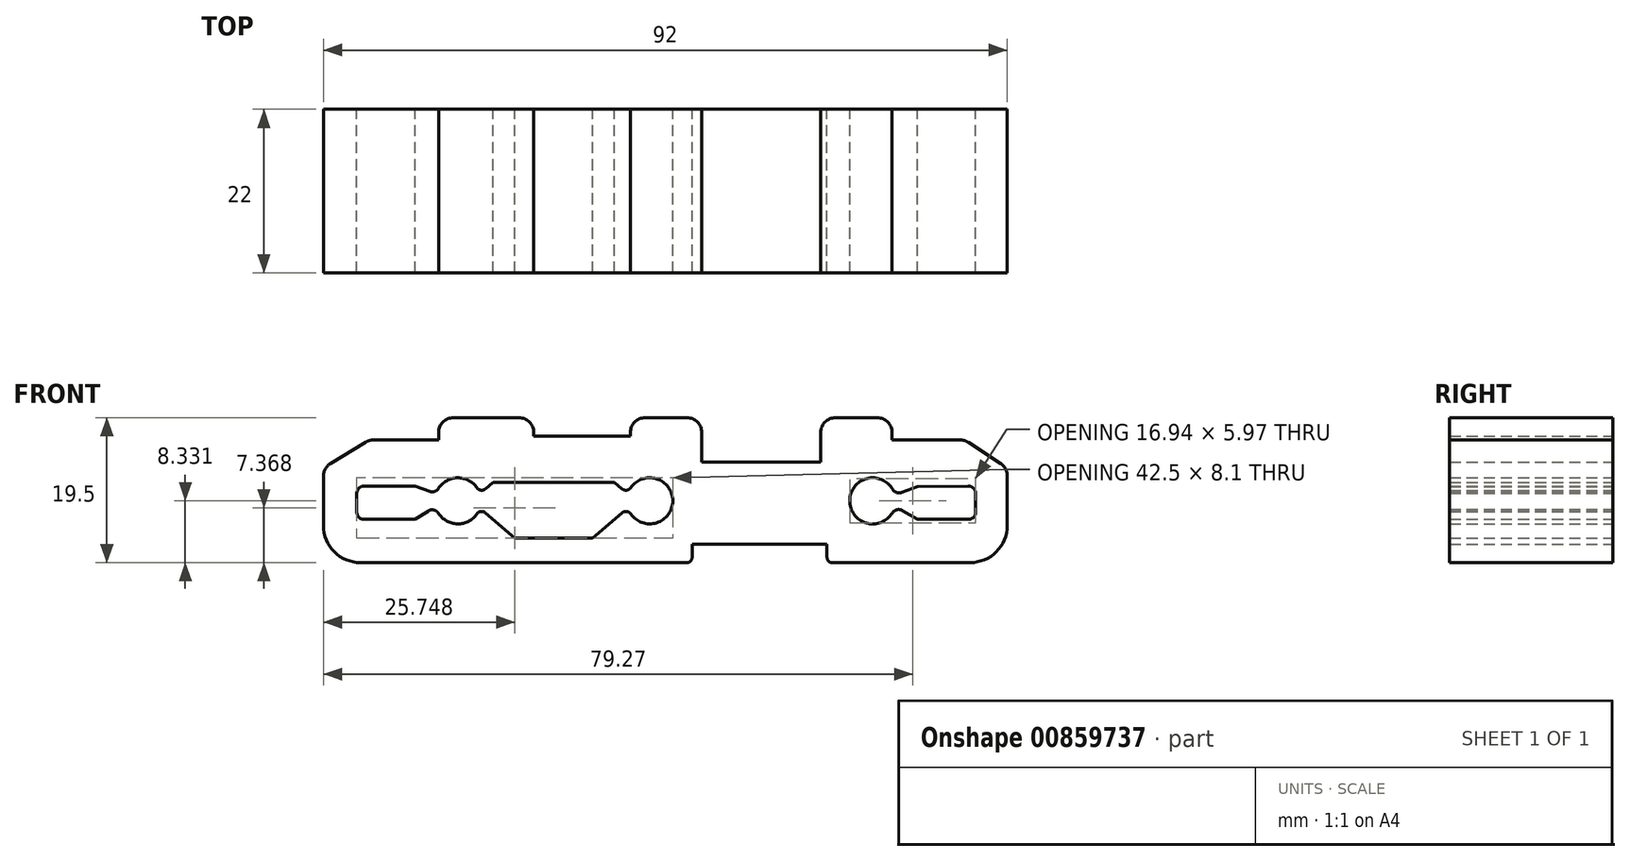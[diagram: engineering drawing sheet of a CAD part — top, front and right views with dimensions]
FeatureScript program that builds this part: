
annotation { "Feature Type Name" : "Feature", "Feature Type Description" : "" }
export const myFeature = defineFeature(function(context is Context, id is Id, definition is map)
    precondition{}
    {
        {
            var Q0;
            Q0=qCreatedBy(makeId("Front.planeOp"),FACE);
            var sketch = newSketch(context, id + "F0", { "sketchPlane" : qUnion([Q0])});
            skLineSegment(sketch, "E0.bottom", {"start": v(-44.05, 9.73) * mm, "end": v(-35.25, 9.73) * mm});
            skLineSegment(sketch, "E0.left", {"start": v(-61.55, 1.86) * mm, "end": v(-61.55, -4.77) * mm});
            skLineSegment(sketch, "E0.right", {"start": v(30.45, 1.9) * mm, "end": v(30.45, -4.77) * mm});
            skLineSegment(sketch, "E1", {"start": v(-46.05, 7.73) * mm, "end": v(-46.05, 6.73) * mm});
            skLineSegment(sketch, "E2", {"start": v(-33.25, 7.73) * mm, "end": v(-33.25, 7.23) * mm});
            skLineSegment(sketch, "E3", {"start": v(-33.25, 7.23) * mm, "end": v(-20.25, 7.23) * mm});
            skLineSegment(sketch, "E4", {"start": v(-20.25, 7.23) * mm, "end": v(-20.25, 7.73) * mm});
            skLineSegment(sketch, "E5", {"start": v(-10.65, 7.73) * mm, "end": v(-10.65, 3.73) * mm});
            skLineSegment(sketch, "E6", {"start": v(-10.65, 3.73) * mm, "end": v(5.35, 3.73) * mm});
            skLineSegment(sketch, "E7", {"start": v(5.35, 3.73) * mm, "end": v(5.35, 7.73) * mm});
            skLineSegment(sketch, "E8", {"start": v(14.95, 7.73) * mm, "end": v(14.95, 6.73) * mm});
            skLineSegment(sketch, "E9", {"start": v(14.95, 6.73) * mm, "end": v(24.11, 6.73) * mm});
            skLineSegment(sketch, "E10", {"start": v(-11.95, -9.07) * mm, "end": v(-11.95, -7.27) * mm});
            skLineSegment(sketch, "E11", {"start": v(6.2, -7.27) * mm, "end": v(6.2, -9.07) * mm});
            skLineSegment(sketch, "E12.trimOffspring", {"start": v(6.3, -9.77) * mm, "end": v(25.45, -9.77) * mm});
            skLineSegment(sketch, "E13.trimOffspring", {"start": v(7.35, 9.73) * mm, "end": v(12.95, 9.73) * mm});
            skLineSegment(sketch, "E14.trimOffspring", {"start": v(-18.25, 9.73) * mm, "end": v(-12.65, 9.73) * mm});
            skLineSegment(sketch, "E15", {"start": v(-46.05, 6.73) * mm, "end": v(-54.82, 6.73) * mm});
            skLineSegment(sketch, "E16", {"start": v(-55.85, 6.44) * mm, "end": v(-60.59, 3.57) * mm});
            skLineSegment(sketch, "E17", {"start": v(25.2, 6.4) * mm, "end": v(29.54, 3.58) * mm});
            skPoint(sketch, "E18.visualSharp", {"position": v(-55.38, 6.73) * mm});
            skArc(sketch, "E18.filletArc", {"start": v(-54.82, 6.73) * mm, "mid": v(-55.35, 6.66) * mm, "end": v(-55.85, 6.44) * mm});
            skPoint(sketch, "E19.visualSharp", {"position": v(-61.55, 2.99) * mm});
            skArc(sketch, "E19.filletArc", {"start": v(-60.59, 3.57) * mm, "mid": v(-61.3, 2.84) * mm, "end": v(-61.55, 1.86) * mm});
            skPoint(sketch, "E20.visualSharp", {"position": v(-46.05, 9.73) * mm});
            skArc(sketch, "E20.filletArc", {"start": v(-44.05, 9.73) * mm, "mid": v(-45.47, 9.15) * mm, "end": v(-46.05, 7.73) * mm});
            skPoint(sketch, "E21.visualSharp", {"position": v(-33.25, 9.73) * mm});
            skArc(sketch, "E21.filletArc", {"start": v(-33.25, 7.73) * mm, "mid": v(-33.84, 9.15) * mm, "end": v(-35.25, 9.73) * mm});
            skPoint(sketch, "E22.visualSharp", {"position": v(-20.25, 9.73) * mm});
            skArc(sketch, "E22.filletArc", {"start": v(-18.25, 9.73) * mm, "mid": v(-19.67, 9.15) * mm, "end": v(-20.25, 7.73) * mm});
            skPoint(sketch, "E23.visualSharp", {"position": v(14.95, 9.73) * mm});
            skArc(sketch, "E23.filletArc", {"start": v(14.95, 7.73) * mm, "mid": v(14.36, 9.15) * mm, "end": v(12.95, 9.73) * mm});
            skPoint(sketch, "E24.visualSharp", {"position": v(24.7, 6.73) * mm});
            skArc(sketch, "E24.filletArc", {"start": v(25.2, 6.4) * mm, "mid": v(24.68, 6.65) * mm, "end": v(24.11, 6.73) * mm});
            skPoint(sketch, "E25.visualSharp", {"position": v(30.45, 2.99) * mm});
            skArc(sketch, "E25.filletArc", {"start": v(30.45, 1.9) * mm, "mid": v(30.2, 2.86) * mm, "end": v(29.54, 3.58) * mm});
            skPoint(sketch, "E26.visualSharp", {"position": v(-10.65, 9.73) * mm});
            skArc(sketch, "E26.filletArc", {"start": v(-10.65, 7.73) * mm, "mid": v(-11.24, 9.15) * mm, "end": v(-12.65, 9.73) * mm});
            skPoint(sketch, "E27.visualSharp", {"position": v(5.35, 9.73) * mm});
            skArc(sketch, "E27.filletArc", {"start": v(7.35, 9.73) * mm, "mid": v(5.93, 9.15) * mm, "end": v(5.35, 7.73) * mm});
            skPoint(sketch, "E28.visualSharp", {"position": v(-61.55, -9.77) * mm});
            skArc(sketch, "E28.filletArc", {"start": v(-61.55, -4.77) * mm, "mid": v(-60.09, -8.3) * mm, "end": v(-56.55, -9.77) * mm});
            skPoint(sketch, "E29.visualSharp", {"position": v(30.45, -9.77) * mm});
            skArc(sketch, "E29.filletArc", {"start": v(25.45, -9.77) * mm, "mid": v(28.98, -8.3) * mm, "end": v(30.45, -4.77) * mm});
            skPoint(sketch, "E30.visualSharp", {"position": v(-12.55, -9.77) * mm});
            skArc(sketch, "E30.filletArc", {"start": v(-12.65, -9.77) * mm, "mid": v(-12.16, -9.56) * mm, "end": v(-11.95, -9.07) * mm});
            skPoint(sketch, "E31.visualSharp", {"position": v(6.2, -9.77) * mm});
            skArc(sketch, "E31.filletArc", {"start": v(6.2, -9.07) * mm, "mid": v(6.4, -9.56) * mm, "end": v(6.9, -9.77) * mm});
            skLineSegment(sketch, "E32", {"start": v(-56.55, -9.77) * mm, "end": v(-12.65, -9.77) * mm});
            skLineSegment(sketch, "E33", {"start": v(-11.95, -7.27) * mm, "end": v(6.2, -7.27) * mm});
            skLineSegment(sketch, "E34", {"start": v(-41.3, -9.77) * mm, "end": v(-41.3, 0.23) * mm, "construction": true});
            skLineSegment(sketch, "E35", {"start": v(-61.55, -1.45) * mm, "end": v(-43.45, -1.45) * mm, "construction": true});
            skLineSegment(sketch, "E36", {"start": v(-43.45, -1.45) * mm, "end": v(-25.32, -1.45) * mm, "construction": true});
            skLineSegment(sketch, "E37", {"start": v(-17.65, -1.45) * mm, "end": v(12.35, -1.45) * mm, "construction": true});
            skArc(sketch, "E38", {"start": v(-46.07, -3.11) * mm, "mid": v(-43.51, -4.55) * mm, "end": v(-40.9, -3.22) * mm});
            skArc(sketch, "E39", {"start": v(-20.2, -3.22) * mm, "mid": v(-14.55, -1.45) * mm, "end": v(-20.2, 0.32) * mm});
            skArc(sketch, "E40", {"start": v(15.03, 0.1) * mm, "mid": v(9.25, -1.4) * mm, "end": v(14.98, -3.09) * mm});
            skLineSegment(sketch, "E41", {"start": v(-56.05, -3.95) * mm, "end": v(-49.2, -3.95) * mm});
            skLineSegment(sketch, "E42", {"start": v(-57.05, -0.45) * mm, "end": v(-57.05, -2.95) * mm});
            skLineSegment(sketch, "E43", {"start": v(-56.05, 0.55) * mm, "end": v(-49.2, 0.55) * mm});
            skLineSegment(sketch, "E44", {"start": v(-49.2, 0.55) * mm, "end": v(-47.27, -0.19) * mm});
            skLineSegment(sketch, "E45", {"start": v(-47.46, -2.81) * mm, "end": v(-49.2, -3.95) * mm});
            skPoint(sketch, "E46.visualSharp", {"position": v(-46.4, -0.51) * mm});
            skArc(sketch, "E46.filletArc", {"start": v(-47.27, -0.19) * mm, "mid": v(-46.6, -0.2) * mm, "end": v(-46.07, 0.21) * mm});
            skPoint(sketch, "E47.visualSharp", {"position": v(-46.47, -2.17) * mm});
            skArc(sketch, "E47.filletArc", {"start": v(-46.07, -3.11) * mm, "mid": v(-46.7, -2.67) * mm, "end": v(-47.46, -2.81) * mm});
            skPoint(sketch, "E48.visualSharp", {"position": v(-57.05, 0.55) * mm});
            skArc(sketch, "E48.filletArc", {"start": v(-56.05, 0.55) * mm, "mid": v(-56.76, 0.26) * mm, "end": v(-57.05, -0.45) * mm});
            skPoint(sketch, "E49.visualSharp", {"position": v(-57.05, -3.95) * mm});
            skArc(sketch, "E49.filletArc", {"start": v(-57.05, -2.95) * mm, "mid": v(-56.76, -3.66) * mm, "end": v(-56.05, -3.95) * mm});
            skLineSegment(sketch, "E50", {"start": v(-49.2, 0.55) * mm, "end": v(-49.2, 1.05) * mm, "construction": true});
            skLineSegment(sketch, "E51", {"start": v(-34.63, 1.05) * mm, "end": v(-34.63, -6.45) * mm, "construction": true});
            skLineSegment(sketch, "E52", {"start": v(-17.65, -1.45) * mm, "end": v(-22.4, -1.45) * mm, "construction": true});
            skPoint(sketch, "E53.end.orphan", {"position": v(-25.32, -4.04) * mm});
            skPoint(sketch, "E54.start.orphan", {"position": v(-25.32, -6.45) * mm});
            skPoint(sketch, "E55.start.orphan", {"position": v(-22.4, 1.05) * mm});
            skLineSegment(sketch, "E56", {"start": v(-22.4, 1.05) * mm, "end": v(-21.38, 0.17) * mm});
            skLineSegment(sketch, "E57", {"start": v(-21.38, -3.07) * mm, "end": v(-25.32, -6.45) * mm});
            skLineSegment(sketch, "E58", {"start": v(-22.4, 1.05) * mm, "end": v(-38.7, 1.05) * mm});
            skLineSegment(sketch, "E59", {"start": v(-38.7, 1.05) * mm, "end": v(-39.73, 0.17) * mm});
            skLineSegment(sketch, "E60", {"start": v(-25.32, -6.45) * mm, "end": v(-35.79, -6.45) * mm});
            skArc(sketch, "E61.trimOffspring", {"start": v(-40.9, 0.32) * mm, "mid": v(-43.51, 1.65) * mm, "end": v(-46.07, 0.21) * mm});
            skLineSegment(sketch, "E62", {"start": v(-39.73, -3.07) * mm, "end": v(-35.79, -6.45) * mm});
            skPoint(sketch, "E63.visualSharp", {"position": v(-40.5, -0.5) * mm});
            skArc(sketch, "E63.filletArc", {"start": v(-40.9, 0.32) * mm, "mid": v(-40.35, -0.02) * mm, "end": v(-39.73, 0.17) * mm});
            skPoint(sketch, "E64.visualSharp", {"position": v(-40.5, -2.4) * mm});
            skArc(sketch, "E64.filletArc", {"start": v(-39.73, -3.07) * mm, "mid": v(-40.35, -2.88) * mm, "end": v(-40.9, -3.22) * mm});
            skPoint(sketch, "E65.visualSharp", {"position": v(-20.6, -0.5) * mm});
            skArc(sketch, "E65.filletArc", {"start": v(-21.38, 0.17) * mm, "mid": v(-20.75, -0.02) * mm, "end": v(-20.2, 0.32) * mm});
            skPoint(sketch, "E66.visualSharp", {"position": v(-20.6, -2.4) * mm});
            skArc(sketch, "E66.filletArc", {"start": v(-20.2, -3.22) * mm, "mid": v(-20.75, -2.88) * mm, "end": v(-21.38, -3.07) * mm});
            skPoint(sketch, "E67.orphan", {"position": v(12.35, -3.95) * mm});
            skLineSegment(sketch, "E68", {"start": v(25.2, -3.95) * mm, "end": v(18.35, -3.95) * mm});
            skLineSegment(sketch, "E69", {"start": v(25.18, 0.54) * mm, "end": v(18.35, 0.46) * mm});
            skLineSegment(sketch, "E70", {"start": v(26.2, -0.46) * mm, "end": v(26.2, -2.95) * mm});
            skLineSegment(sketch, "E71", {"start": v(26.2, -1.7) * mm, "end": v(18.35, -1.7) * mm, "construction": true});
            skLineSegment(sketch, "E72", {"start": v(18.35, 0.46) * mm, "end": v(16.25, -0.33) * mm});
            skLineSegment(sketch, "E73", {"start": v(16.34, -2.76) * mm, "end": v(18.35, -3.95) * mm});
            skPoint(sketch, "E74.visualSharp", {"position": v(15.35, -0.67) * mm});
            skArc(sketch, "E74.filletArc", {"start": v(15.03, 0.1) * mm, "mid": v(15.56, -0.34) * mm, "end": v(16.25, -0.33) * mm});
            skPoint(sketch, "E75.visualSharp", {"position": v(15.36, -2.17) * mm});
            skArc(sketch, "E75.filletArc", {"start": v(16.34, -2.76) * mm, "mid": v(15.6, -2.64) * mm, "end": v(14.98, -3.09) * mm});
            skPoint(sketch, "E76.visualSharp", {"position": v(26.2, 0.55) * mm});
            skArc(sketch, "E76.filletArc", {"start": v(26.2, -0.46) * mm, "mid": v(25.9, 0.25) * mm, "end": v(25.18, 0.54) * mm});
            skPoint(sketch, "E77.visualSharp", {"position": v(26.2, -3.95) * mm});
            skArc(sketch, "E77.filletArc", {"start": v(25.2, -3.95) * mm, "mid": v(25.9, -3.66) * mm, "end": v(26.2, -2.95) * mm});
            skSolve(sketch);
        }
        {
            var Q0;
            Q0=makeQuery(id+"F0.imprint","IMPRINT",FACE,{"disambiguationData":[TD([[makeQuery(id+"F0.imprint","IMPRINT",EDGE,{"derivedFrom":sQuery(id+"F0.wireOp",EDGE,"E0.bottom")}),-1.0]])]});
            extrude(context, id + "F1", {"entities" : qUnion([Q0]), "depth" : 22 * mm, "offsetDistance" : 25 * mm});
        }
    });
